# Revit family: NBS_DudleyIndustriesLimited_PprTwlDpnsrs_CentrefeedPaperTowelDispenser_PlasmaRange_79037PS
name_source: partatom
category: Specialty Equipment
units: mm (PartAtom-declared; Revit-internal decimal feet)

## family parameters
Cut with Voids When Loaded = No
Host = Face
Part Type = Normal
Room Calculation Point = No
Round Connector Dimension = Use Diameter
Shared = No

## types (1)
- 78037PS
    AssetType = Type
    BIMObjectName = NBS_DudleyIndustriesLimited_PaperTowelDispensers_CentrefeedPaperTowelDispenser_PlasmaRange_78037PS
    Category = Pr_40_70_22_62:Paper towel dispensers
    Color = Polished / Brushed
    Default Elevation = 1150 mm
    Description = Stylish stainless steel centrefeed paper towel dispenser with brushed finish
    DispenserDepth = 216 mm  [stored 0.708661 ft]
    DispenserHeight = 388 mm  [stored 1.27297 ft]
    DispenserMaterial = NBS_DudleyIndustries_StainlessSteel_Polished
    DispenserWidth = 211 mm  [stored 0.692257 ft]
    Features = Stylish, brushed stainless steel-constructed centre-feed dispenser,Suitable for perforated and non-perforated paper,Houses a full centre feed roll for both perforated and non-perforated paper,Recessed locking mechanism to secure contents,Full seam-welded fabrication,Fixing kit included
    Finish = Polished / Brushed
    HasProtectiveEarth = No
    IfcExportAs = IfcFurnitureType
    IfcExportType = NOTDEFINED
    IsBuiltIn = No
    ManufacturerName = Dudley Industries Limited
    ManufacturerURL = www.dudleyindustries.com
    Material = Stainless Steel
    ModelNumber = 78037PS
    ModelReference = Centrefeed Paper Towel Dispenser Plasma Range 79037P
    NBSCertification = www.nationalbimlibrary.com/cert/0czth1w2
    NBSDescription = Paper towel dispensers
    NBSReference = 45-35-72/344
    Name = PaperTowelDispensers_CentrefeedPaperTowelDispenser_PlasmaRange_79037PS_DudleyIndustriesLimited_NBS
    NominalDepth = 216 mm  [stored 0.708661 ft]
    NominalHeight = 388 mm  [stored 1.27297 ft]
    NominalLength = 211 mm  [stored 0.692257 ft]
    NominalWidth = 211 mm  [stored 0.692257 ft]
    NumberOfPoles = 0
    PowerFactor = 0
    Size = 388mm x 211mm x 216mm
    Status = UNSET
    Uniclass2015Code = Pr_40_70_22_62
    Uniclass2015Title = Paper towel dispensers
    Uniclass2015Version = Products v1.22
    Version = 1
    WarrantyDurationUnit = year

note: [stored X ft] marks values corroborated as IEEE doubles in the binary element streams (Revit-internal decimal feet)

## geometry (parser evidence)
native form markers: Sweep x2
no freeform markers — native parametric forms only
